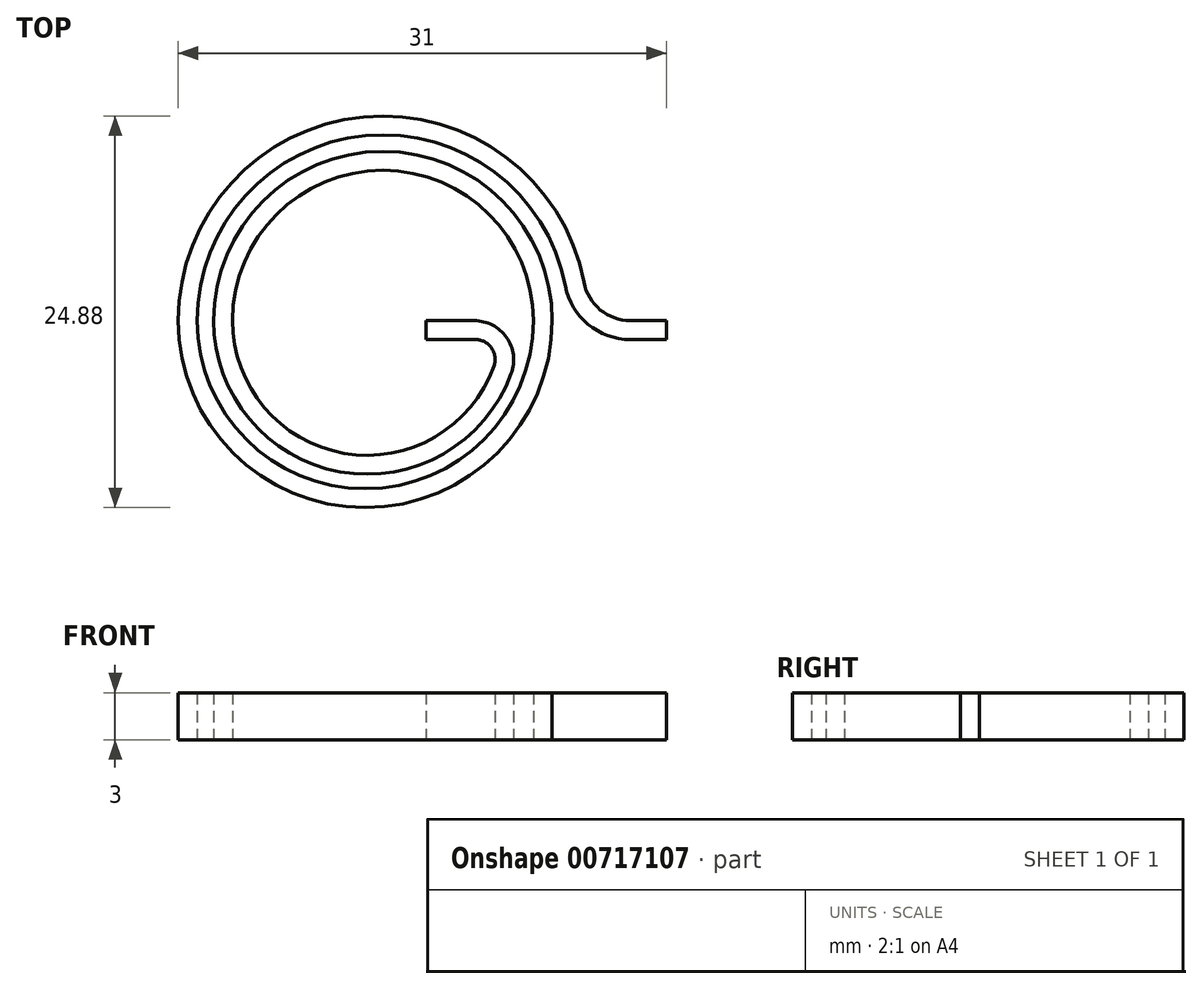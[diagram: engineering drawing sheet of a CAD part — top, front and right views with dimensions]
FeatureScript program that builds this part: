
annotation { "Feature Type Name" : "Feature", "Feature Type Description" : "" }
export const myFeature = defineFeature(function(context is Context, id is Id, definition is map)
    precondition{}
    {
        {
            var Q0;
            Q0=qCreatedBy(makeId("Top.planeOp"),FACE);
            var sketch = newSketch(context, id + "F0", { "sketchPlane" : qUnion([Q0])});
            skArc(sketch, "E0", {"start": v(12.77, 2.44) * mm, "mid": v(-1.22, 12.94) * mm, "end": v(-13, 0) * mm});
            skArc(sketch, "E1", {"start": v(10.75, 0) * mm, "mid": v(0, 10.75) * mm, "end": v(-10.75, 0) * mm});
            skLineSegment(sketch, "E2", {"start": v(15.72, 0) * mm, "end": v(18, 0) * mm});
            skLineSegment(sketch, "E3", {"start": v(5.8, 0) * mm, "end": v(2.75, 0) * mm});
            skArc(sketch, "E4", {"start": v(-13, 0) * mm, "mid": v(-1.12, -11.88) * mm, "end": v(10.75, 0) * mm});
            skArc(sketch, "E5", {"start": v(-10.75, 0) * mm, "mid": v(-2.7, -9.6) * mm, "end": v(8.15, -3.36) * mm});
            skPoint(sketch, "E6.visualSharp", {"position": v(13, 0) * mm});
            skArc(sketch, "E6.filletArc", {"start": v(12.77, 2.44) * mm, "mid": v(13.8, 0.69) * mm, "end": v(15.72, 0) * mm});
            skPoint(sketch, "E7.visualSharp", {"position": v(8.75, 0) * mm});
            skArc(sketch, "E7.filletArc", {"start": v(8.15, -3.36) * mm, "mid": v(7.86, -1.07) * mm, "end": v(5.8, 0) * mm});
            skLineSegment(sketch, "E8.0", {"start": v(15.72, -1.2) * mm, "end": v(18, -1.2) * mm});
            skArc(sketch, "E8.1", {"start": v(11.6, 2.21) * mm, "mid": v(13.04, -0.24) * mm, "end": v(15.72, -1.2) * mm});
            skArc(sketch, "E8.2", {"start": v(-9.55, 0) * mm, "mid": v(-2.46, -8.43) * mm, "end": v(7.05, -2.87) * mm});
            skArc(sketch, "E8.3", {"start": v(9.55, 0) * mm, "mid": v(0, 9.55) * mm, "end": v(-9.55, 0) * mm});
            skArc(sketch, "E8.4", {"start": v(-11.8, 0) * mm, "mid": v(-1.13, -10.68) * mm, "end": v(9.55, 0) * mm});
            skArc(sketch, "E8.5", {"start": v(11.6, 2.21) * mm, "mid": v(-1.11, 11.75) * mm, "end": v(-11.8, 0) * mm});
            skLineSegment(sketch, "E9.0", {"start": v(5.88, -1.2) * mm, "end": v(2.75, -1.2) * mm});
            skLineSegment(sketch, "E10", {"start": v(2.75, 0) * mm, "end": v(2.75, -1.2) * mm});
            skArc(sketch, "E11.filletArc", {"start": v(7.05, -2.87) * mm, "mid": v(6.9, -1.73) * mm, "end": v(5.88, -1.2) * mm});
            skLineSegment(sketch, "E12", {"start": v(18, 0) * mm, "end": v(18, -1.2) * mm});
            skSolve(sketch);
        }
        {
            var Q0;
            Q0 = qSketchRegion(id + "F0", true);
            extrude(context, id + "F1", {"entities" : qUnion([Q0]), "depth" : 3 * mm, "offsetDistance" : 25 * mm});
        }
    });
